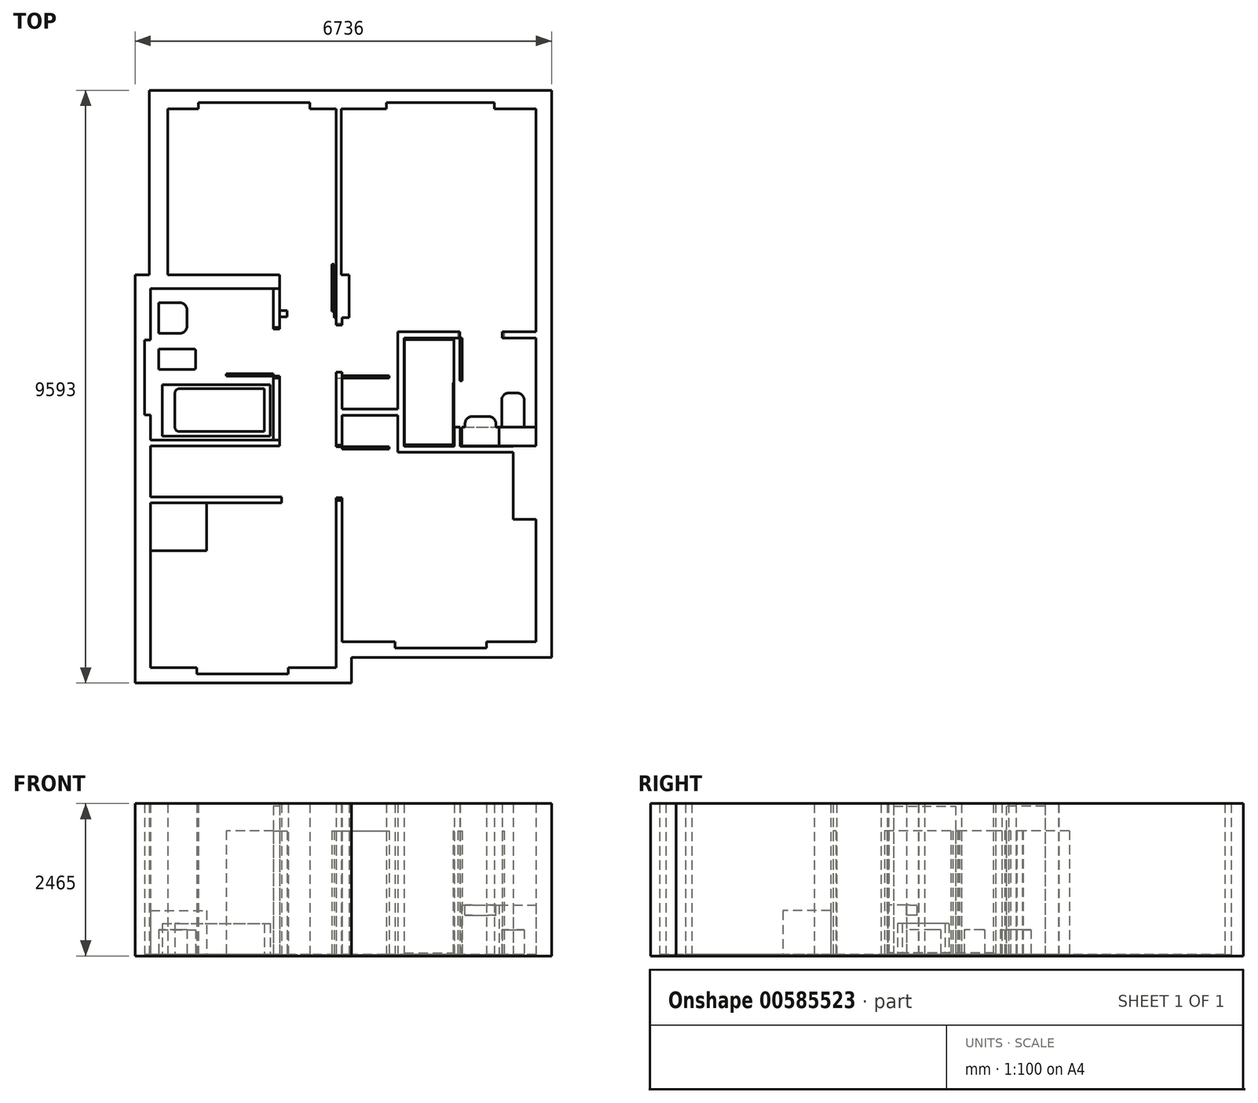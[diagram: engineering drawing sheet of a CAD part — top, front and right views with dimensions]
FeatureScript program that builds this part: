
annotation { "Feature Type Name" : "Feature", "Feature Type Description" : "" }
export const myFeature = defineFeature(function(context is Context, id is Id, definition is map)
    precondition{}
    {
        {
            var Q0;
            Q0=qCreatedBy(makeId("Top.planeOp"),FACE);
            var sketch = newSketch(context, id + "F0", { "sketchPlane" : qUnion([Q0])});
            skLineSegment(sketch, "E0", {"start": v(0, 0) * mm, "end": v(749, 0) * mm});
            skLineSegment(sketch, "E1", {"start": v(749, 0) * mm, "end": v(749, -100) * mm});
            skLineSegment(sketch, "E2", {"start": v(749, -100) * mm, "end": v(2229, -100) * mm});
            skLineSegment(sketch, "E3", {"start": v(2229, -100) * mm, "end": v(2229, 0) * mm});
            skLineSegment(sketch, "E4", {"start": v(2229, 0) * mm, "end": v(3000, 0) * mm});
            skLineSegment(sketch, "E5", {"start": v(3000, 0) * mm, "end": v(3000, 2705) * mm});
            skLineSegment(sketch, "E6", {"start": v(3000, 2705) * mm, "end": v(3100, 2705) * mm});
            skLineSegment(sketch, "E7", {"start": v(3100, 2705) * mm, "end": v(3100, 418) * mm});
            skLineSegment(sketch, "E8", {"start": v(3100, 418) * mm, "end": v(3954, 418) * mm});
            skLineSegment(sketch, "E9", {"start": v(3954, 418) * mm, "end": v(3954, 318) * mm});
            skLineSegment(sketch, "E10", {"start": v(3954, 318) * mm, "end": v(5437, 318) * mm});
            skLineSegment(sketch, "E11", {"start": v(5437, 318) * mm, "end": v(5437, 418) * mm});
            skLineSegment(sketch, "E12", {"start": v(5437, 418) * mm, "end": v(6236, 418) * mm});
            skLineSegment(sketch, "E13", {"start": v(6236, 418) * mm, "end": v(6236, 2400) * mm});
            skLineSegment(sketch, "E14", {"start": v(6236, 2400) * mm, "end": v(5866, 2400) * mm});
            skLineSegment(sketch, "E15", {"start": v(5866, 2400) * mm, "end": v(5866, 3585) * mm});
            skLineSegment(sketch, "E16", {"start": v(5866, 3585) * mm, "end": v(6236, 3585) * mm});
            skLineSegment(sketch, "E17", {"start": v(6236, 3585) * mm, "end": v(6236, 9043) * mm});
            skLineSegment(sketch, "E18", {"start": v(6236, 9043) * mm, "end": v(5559, 9043) * mm});
            skLineSegment(sketch, "E19", {"start": v(5559, 9043) * mm, "end": v(5559, 9143) * mm});
            skLineSegment(sketch, "E20", {"start": v(5559, 9143) * mm, "end": v(3814, 9143) * mm});
            skLineSegment(sketch, "E21", {"start": v(3814, 9143) * mm, "end": v(3814, 9043) * mm});
            skLineSegment(sketch, "E22", {"start": v(3814, 9043) * mm, "end": v(3085, 9043) * mm});
            skLineSegment(sketch, "E23", {"start": v(3085, 9043) * mm, "end": v(3085, 6354) * mm});
            skLineSegment(sketch, "E24", {"start": v(3085, 6354) * mm, "end": v(3210, 6354) * mm});
            skLineSegment(sketch, "E25", {"start": v(3210, 6354) * mm, "end": v(3210, 5663) * mm});
            skLineSegment(sketch, "E26", {"start": v(3210, 5663) * mm, "end": v(3100, 5663) * mm});
            skLineSegment(sketch, "E27", {"start": v(3100, 5663) * mm, "end": v(3100, 3603) * mm});
            skLineSegment(sketch, "E28", {"start": v(3100, 3603) * mm, "end": v(3000, 3603) * mm});
            skLineSegment(sketch, "E29", {"start": v(3000, 3603) * mm, "end": v(3000, 9043) * mm});
            skLineSegment(sketch, "E30", {"start": v(3000, 9043) * mm, "end": v(2575, 9043) * mm});
            skLineSegment(sketch, "E31", {"start": v(2575, 9043) * mm, "end": v(2575, 9143) * mm});
            skLineSegment(sketch, "E32", {"start": v(2575, 9143) * mm, "end": v(775, 9143) * mm});
            skLineSegment(sketch, "E33", {"start": v(775, 9143) * mm, "end": v(775, 9043) * mm});
            skLineSegment(sketch, "E34", {"start": v(775, 9043) * mm, "end": v(280, 9043) * mm});
            skLineSegment(sketch, "E35", {"start": v(280, 9043) * mm, "end": v(280, 6353) * mm});
            skLineSegment(sketch, "E36", {"start": v(280, 6353) * mm, "end": v(2086, 6353) * mm});
            skLineSegment(sketch, "E37", {"start": v(2086, 6353) * mm, "end": v(2086, 6134) * mm});
            skLineSegment(sketch, "E38", {"start": v(2086, 6134) * mm, "end": v(1, 6134) * mm});
            skLineSegment(sketch, "E39", {"start": v(1, 6134) * mm, "end": v(1, 5299) * mm});
            skLineSegment(sketch, "E40", {"start": v(1, 5299) * mm, "end": v(-99, 5299) * mm});
            skLineSegment(sketch, "E41", {"start": v(-99, 5299) * mm, "end": v(-99, 4091) * mm});
            skLineSegment(sketch, "E42", {"start": v(-99, 4091) * mm, "end": v(1, 4091) * mm});
            skLineSegment(sketch, "E43", {"start": v(1, 4091) * mm, "end": v(1, 3685) * mm});
            skLineSegment(sketch, "E44", {"start": v(1, 3685) * mm, "end": v(2086, 3685) * mm});
            skLineSegment(sketch, "E45", {"start": v(2086, 3685) * mm, "end": v(2086, 3585) * mm});
            skLineSegment(sketch, "E46", {"start": v(2086, 3585) * mm, "end": v(0, 3585) * mm});
            skLineSegment(sketch, "E47", {"start": v(0, 3585) * mm, "end": v(0, 2765) * mm});
            skLineSegment(sketch, "E48", {"start": v(0, 2665) * mm, "end": v(6.12, 2665) * mm});
            skLineSegment(sketch, "E49", {"start": v(2119, 2665) * mm, "end": v(2119, 2765) * mm});
            skLineSegment(sketch, "E50", {"start": v(2119, 2765) * mm, "end": v(0, 2765) * mm});
            skLineSegment(sketch, "E51", {"start": v(0, 1892) * mm, "end": v(906, 1892) * mm, "construction": true});
            skLineSegment(sketch, "E52", {"start": v(906, 1892) * mm, "end": v(906, 2665) * mm, "construction": true});
            skLineSegment(sketch, "E53.12", {"start": v(3250, 168) * mm, "end": v(3704, 168) * mm});
            skLineSegment(sketch, "E53.13", {"start": v(3250, -250) * mm, "end": v(3250, 168) * mm});
            skLineSegment(sketch, "E53.14", {"start": v(2479, -250) * mm, "end": v(3250, -250) * mm});
            skLineSegment(sketch, "E53.15", {"start": v(-250, -250) * mm, "end": v(499, -250) * mm});
            skLineSegment(sketch, "E53.19", {"start": v(5687, 168) * mm, "end": v(6486, 168) * mm});
            skLineSegment(sketch, "E53.20", {"start": v(6486, 168) * mm, "end": v(6486, 2650) * mm});
            skLineSegment(sketch, "E53.24", {"start": v(6486, 3335) * mm, "end": v(6486, 9343) * mm});
            skLineSegment(sketch, "E53.28", {"start": v(-250, 6353) * mm, "end": v(-250, -250) * mm});
            skLineSegment(sketch, "E54.0", {"start": v(-20, 9343) * mm, "end": v(-20, 6353) * mm});
            skLineSegment(sketch, "E54.1", {"start": v(775, 9343) * mm, "end": v(-20, 9343) * mm});
            skLineSegment(sketch, "E55", {"start": v(775, 9343) * mm, "end": v(6486, 9343) * mm});
            skLineSegment(sketch, "E56", {"start": v(0, 2765) * mm, "end": v(0, 2765) * mm});
            skLineSegment(sketch, "E57", {"start": v(0, 2665) * mm, "end": v(0, 0) * mm});
            skLineSegment(sketch, "E58", {"start": v(6.12, 2665) * mm, "end": v(2119, 2665) * mm});
            skLineSegment(sketch, "E59", {"start": v(499, -250) * mm, "end": v(2479, -250) * mm});
            skLineSegment(sketch, "E60", {"start": v(3704, 168) * mm, "end": v(5687, 168) * mm});
            skLineSegment(sketch, "E61", {"start": v(6486, 3335) * mm, "end": v(6486, 2650) * mm});
            skLineSegment(sketch, "E62", {"start": v(-250, 6353) * mm, "end": v(-20, 6353) * mm});
            skSolve(sketch);
        }
        {
            var Q0;
            Q0=makeQuery(id+"F0.imprint","IMPRINT",FACE,{"disambiguationData":[TD([[makeQuery(id+"F0.imprint","IMPRINT",EDGE,{"derivedFrom":sQuery(id+"F0.wireOp",EDGE,"E0")}),1.0]])]});
            var sketch = newSketch(context, id + "F1", { "sketchPlane" : qUnion([Q0])});
            skLineSegment(sketch, "E63", {"start": v(3100, 4083) * mm, "end": v(4000, 4083) * mm});
            skLineSegment(sketch, "E64", {"start": v(4000, 4083) * mm, "end": v(4000, 3483) * mm});
            skLineSegment(sketch, "E65", {"start": v(4000, 3483) * mm, "end": v(5866, 3483) * mm});
            skLineSegment(sketch, "E66", {"start": v(4000, 4183) * mm, "end": v(4000, 5433) * mm});
            skLineSegment(sketch, "E67", {"start": v(4000, 5433) * mm, "end": v(6236, 5433) * mm});
            skLineSegment(sketch, "E68", {"start": v(6236, 5333) * mm, "end": v(4100, 5333) * mm});
            skLineSegment(sketch, "E69", {"start": v(4100, 5333) * mm, "end": v(4100, 3583) * mm});
            skLineSegment(sketch, "E70", {"start": v(5866, 3583) * mm, "end": v(5866, 3483) * mm});
            skLineSegment(sketch, "E71", {"start": v(6236, 5333) * mm, "end": v(6236, 5433) * mm});
            skLineSegment(sketch, "E72", {"start": v(3100, 4183) * mm, "end": v(3100, 4083) * mm});
            skLineSegment(sketch, "E73", {"start": v(4100, 3583) * mm, "end": v(4910, 3583) * mm});
            skLineSegment(sketch, "E74.bottom", {"start": v(4105, 5308) * mm, "end": v(4905, 5308) * mm, "construction": true});
            skLineSegment(sketch, "E74.top", {"start": v(4105, 3608) * mm, "end": v(4905, 3608) * mm, "construction": true});
            skLineSegment(sketch, "E74.left", {"start": v(4105, 5308) * mm, "end": v(4105, 3608) * mm, "construction": true});
            skLineSegment(sketch, "E74.right", {"start": v(4905, 5308) * mm, "end": v(4905, 3478) * mm, "construction": true});
            skLineSegment(sketch, "E75", {"start": v(4000, 4183) * mm, "end": v(3100, 4183) * mm});
            skLineSegment(sketch, "E76.bottom", {"start": v(5109.15, 4345.6) * mm, "end": v(5109.15, 5095.6) * mm, "construction": true});
            skLineSegment(sketch, "E76.top", {"start": v(6234.15, 4345.6) * mm, "end": v(6234.15, 5095.6) * mm, "construction": true});
            skLineSegment(sketch, "E76.left", {"start": v(5109.15, 4345.6) * mm, "end": v(6234.15, 4345.6) * mm, "construction": true});
            skLineSegment(sketch, "E76.right", {"start": v(5109.15, 5095.6) * mm, "end": v(6234.15, 5095.6) * mm, "construction": true});
            skLineSegment(sketch, "E77.bottom", {"start": v(5808.64, 3997.9) * mm, "end": v(5808.64, 3497.9) * mm, "construction": true});
            skLineSegment(sketch, "E77.top", {"start": v(5048.64, 3997.9) * mm, "end": v(5048.64, 3497.9) * mm, "construction": true});
            skLineSegment(sketch, "E77.left", {"start": v(5808.64, 3997.9) * mm, "end": v(5048.64, 3997.9) * mm, "construction": true});
            skLineSegment(sketch, "E77.right", {"start": v(5808.64, 3497.9) * mm, "end": v(5048.64, 3497.9) * mm, "construction": true});
            skLineSegment(sketch, "E78", {"start": v(5109.15, 4720.6) * mm, "end": v(6234.15, 4720.6) * mm, "construction": true});
            skLineSegment(sketch, "E79", {"start": v(5428.64, 3997.9) * mm, "end": v(5428.64, 3497.9) * mm, "construction": true});
            skLineSegment(sketch, "E80.bottom", {"start": v(4910, 3890) * mm, "end": v(5010, 3890) * mm});
            skLineSegment(sketch, "E80.left", {"start": v(4910, 3890) * mm, "end": v(4910, 3583) * mm});
            skLineSegment(sketch, "E80.right", {"start": v(5010, 3890) * mm, "end": v(5010, 3583) * mm});
            skLineSegment(sketch, "E81.trimOffspring", {"start": v(5010, 3583) * mm, "end": v(5866, 3583) * mm});
            skSolve(sketch);
        }
        {
            var Q0;
            Q0=qCreatedBy(makeId("Top.planeOp"),FACE);
            var sketch = newSketch(context, id + "F2", { "sketchPlane" : qUnion([Q0])});
            skLineSegment(sketch, "E82.bottom", {"start": v(3000, 5545) * mm, "end": v(3100, 5545) * mm});
            skLineSegment(sketch, "E82.top", {"start": v(3000, 4783) * mm, "end": v(3100, 4783) * mm});
            skLineSegment(sketch, "E82.left", {"start": v(3000, 5545) * mm, "end": v(3000, 4783) * mm});
            skLineSegment(sketch, "E82.right", {"start": v(3100, 5545) * mm, "end": v(3100, 4783) * mm});
            skSolve(sketch);
        }
        {
            var Q0;
            Q0=qCreatedBy(makeId("Top.planeOp"),FACE);
            var sketch = newSketch(context, id + "F3", { "sketchPlane" : qUnion([Q0])});
            skLineSegment(sketch, "E83.bottom", {"start": v(5000, 5433) * mm, "end": v(5690, 5433) * mm});
            skLineSegment(sketch, "E83.top", {"start": v(5000, 5333) * mm, "end": v(5690, 5333) * mm});
            skLineSegment(sketch, "E83.left", {"start": v(5000, 5433) * mm, "end": v(5000, 5333) * mm});
            skLineSegment(sketch, "E83.right", {"start": v(5690, 5433) * mm, "end": v(5690, 5333) * mm});
            skSolve(sketch);
        }
        {
            var Q0;
            Q0=qCreatedBy(makeId("Top.planeOp"),FACE);
            var sketch = newSketch(context, id + "F4", { "sketchPlane" : qUnion([Q0])});
            skLineSegment(sketch, "E84.0", {"start": v(4105, 5308) * mm, "end": v(4905, 5308) * mm});
            skLineSegment(sketch, "E85.0", {"start": v(4105, 5308) * mm, "end": v(4105, 3608) * mm});
            skLineSegment(sketch, "E86.0", {"start": v(4105, 3608) * mm, "end": v(4905, 3608) * mm});
            skLineSegment(sketch, "E87.0", {"start": v(4905, 5308) * mm, "end": v(4905, 3478) * mm});
            skLineSegment(sketch, "E88.bottom", {"start": v(5454.15, 4903.1) * mm, "end": v(5889.15, 4903.1) * mm});
            skLineSegment(sketch, "E88.top", {"start": v(5454.15, 4538.1) * mm, "end": v(5889.15, 4538.1) * mm});
            skLineSegment(sketch, "E88.left", {"start": v(5374.15, 4823.1) * mm, "end": v(5374.15, 4618.1) * mm});
            skLineSegment(sketch, "E88.right", {"start": v(5929.15, 4863.1) * mm, "end": v(5929.15, 4578.1) * mm});
            skLineSegment(sketch, "E89", {"start": v(5374.15, 4720.6) * mm, "end": v(5866, 4720.6) * mm, "construction": true});
            skPoint(sketch, "E90.visualSharp", {"position": v(5374.15, 4903.1) * mm});
            skArc(sketch, "E90.filletArc", {"start": v(5454.15, 4903.1) * mm, "mid": v(5397.58, 4879.66) * mm, "end": v(5374.15, 4823.1) * mm});
            skPoint(sketch, "E91.visualSharp", {"position": v(5374.15, 4538.1) * mm});
            skArc(sketch, "E91.filletArc", {"start": v(5374.15, 4618.1) * mm, "mid": v(5397.58, 4561.53) * mm, "end": v(5454.15, 4538.1) * mm});
            skPoint(sketch, "E92.visualSharp", {"position": v(5866, 4538.1) * mm});
            skArc(sketch, "E92.filletArc", {"start": v(5889.15, 4538.1) * mm, "mid": v(5917.44, 4549.81) * mm, "end": v(5929.15, 4578.1) * mm});
            skPoint(sketch, "E93.visualSharp", {"position": v(5866, 4903.1) * mm});
            skArc(sketch, "E93.filletArc", {"start": v(5929.15, 4863.1) * mm, "mid": v(5917.44, 4891.38) * mm, "end": v(5889.15, 4903.1) * mm});
            skLineSegment(sketch, "E94.bottom", {"start": v(5678.64, 3632.47) * mm, "end": v(5678.64, 3277.47) * mm});
            skLineSegment(sketch, "E94.top", {"start": v(5178.64, 3632.47) * mm, "end": v(5178.64, 3277.47) * mm});
            skLineSegment(sketch, "E94.left", {"start": v(5578.64, 3732.47) * mm, "end": v(5278.64, 3732.47) * mm});
            skLineSegment(sketch, "E94.right", {"start": v(5678.64, 3277.47) * mm, "end": v(5178.64, 3277.47) * mm});
            skLineSegment(sketch, "E95", {"start": v(5428.64, 3732.47) * mm, "end": v(5428.64, 3277.47) * mm, "construction": true});
            skPoint(sketch, "E96.visualSharp", {"position": v(5678.64, 3732.47) * mm});
            skArc(sketch, "E96.filletArc", {"start": v(5678.64, 3632.47) * mm, "mid": v(5649.35, 3703.18) * mm, "end": v(5578.64, 3732.47) * mm});
            skPoint(sketch, "E97.visualSharp", {"position": v(5178.64, 3732.47) * mm});
            skArc(sketch, "E97.filletArc", {"start": v(5278.64, 3732.47) * mm, "mid": v(5207.93, 3703.18) * mm, "end": v(5178.64, 3632.47) * mm});
            skCircle(sketch, "E98", {"center": v(5428.64, 3482.47) * mm, "radius": 38 * mm});
            skCircle(sketch, "E99", {"center": v(5428.64, 2896.26) * mm, "radius": 12.5 * mm});
            skSolve(sketch);
        }
        {
            var Q0;
            Q0=qCreatedBy(makeId("Top.planeOp"),FACE);
            var sketch = newSketch(context, id + "F5", { "sketchPlane" : qUnion([Q0])});
            skLineSegment(sketch, "E100.bottom", {"start": v(2086, 3685) * mm, "end": v(1986, 3685) * mm});
            skLineSegment(sketch, "E100.top", {"start": v(2086, 4685) * mm, "end": v(1986, 4685) * mm});
            skLineSegment(sketch, "E100.left", {"start": v(2086, 3685) * mm, "end": v(2086, 4685) * mm});
            skLineSegment(sketch, "E100.right", {"start": v(1986, 3685) * mm, "end": v(1986, 4685) * mm});
            skLineSegment(sketch, "E101.bottom", {"start": v(1986, 6134) * mm, "end": v(2086, 6134) * mm});
            skLineSegment(sketch, "E101.top", {"start": v(1986, 5507) * mm, "end": v(2086, 5507) * mm});
            skLineSegment(sketch, "E101.left", {"start": v(1986, 6134) * mm, "end": v(1986, 5507) * mm});
            skLineSegment(sketch, "E101.right", {"start": v(2086, 6134) * mm, "end": v(2086, 5507) * mm});
            skSolve(sketch);
        }
        {
            var Q0;
            Q0=makeQuery(id+"F0.imprint","IMPRINT",FACE,{"disambiguationData":[TD([[makeQuery(id+"F0.imprint","IMPRINT",EDGE,{"derivedFrom":sQuery(id+"F0.wireOp",EDGE,"E0")}),-1.0]])]});
            extrude(context, id + "F6", {"entities" : qUnion([Q0]), "depth" : 2440 * mm, "offsetDistance" : 25 * mm});
        }
        {
            var Q0;
            Q0 = qSketchRegion(id + "F1", true);
            var Q1;
            Q1=makeQuery(id+"F0.imprint","IMPRINT",FACE,{"disambiguationData":[TD([[makeQuery(id+"F0.imprint","IMPRINT",EDGE,{"derivedFrom":sQuery(id+"F0.wireOp",EDGE,"E0")}),-1.0]])]});
            var Q2;
            Q2=makeQuery(id+"F0.imprint","IMPRINT",FACE,{"disambiguationData":[TD([[makeQuery(id+"F0.imprint","IMPRINT",EDGE,{"derivedFrom":sQuery(id+"F0.wireOp",EDGE,"E0")}),1.0]])]});
            var Q3;
            Q3=sQuery(id+"F0.wireOp",EDGE,"E53.28");
            var Q4;
            Q4=sQuery(id+"F0.wireOp",EDGE,"E53.15");
            var Q5;
            Q5=sQuery(id+"F0.wireOp",EDGE,"E59");
            var Q6;
            Q6=sQuery(id+"F0.wireOp",EDGE,"E53.14");
            var Q7;
            Q7=sQuery(id+"F0.wireOp",EDGE,"E53.13");
            var Q8;
            Q8=sQuery(id+"F0.wireOp",EDGE,"E53.19");
            var Q9;
            Q9=sQuery(id+"F0.wireOp",EDGE,"E60");
            var Q10;
            Q10=sQuery(id+"F0.wireOp",EDGE,"E53.12");
            var Q11;
            Q11=sQuery(id+"F0.wireOp",EDGE,"E53.20");
            var Q12;
            Q12=sQuery(id+"F0.wireOp",EDGE,"E61");
            var Q13;
            Q13=sQuery(id+"F0.wireOp",EDGE,"E53.24");
            var Q14;
            Q14=sQuery(id+"F0.wireOp",EDGE,"E55");
            var Q15;
            Q15=sQuery(id+"F0.wireOp",EDGE,"E54.1");
            var Q16;
            Q16=sQuery(id+"F0.wireOp",EDGE,"E62");
            var Q17;
            Q17=sQuery(id+"F0.wireOp",EDGE,"E54.0");
            extrude(context, id + "F7", {"entities" : qUnion([Q0, Q1, Q2]), "operationType" : NewBodyOperationType.ADD, "surfaceEntities" : qUnion([Q3, Q4, Q5, Q6, Q7, Q8, Q9, Q10, Q11, Q12, Q13, Q14, Q15, Q16, Q17]), "oppositeDirection" : true, "depth" : 25 * mm, "offsetDistance" : 25 * mm});
        }
        {
            var Q0;
            Q0 = qSketchRegion(id + "F1", true);
            extrude(context, id + "F8", {"entities" : qUnion([Q0]), "operationType" : NewBodyOperationType.ADD, "depth" : 2440 * mm, "offsetDistance" : 25 * mm});
        }
        {
            var Q0;
            Q0 = qSketchRegion(id + "F2", true);
            extrude(context, id + "F9", {"entities" : qUnion([Q0]), "operationType" : NewBodyOperationType.REMOVE, "depth" : 3100 * mm, "offsetDistance" : 25 * mm});
        }
        {
            var Q0;
            Q0 = qSketchRegion(id + "F3", true);
            extrude(context, id + "F10", {"entities" : qUnion([Q0]), "operationType" : NewBodyOperationType.REMOVE, "depth" : 3100 * mm, "offsetDistance" : 25 * mm});
        }
        {
            var Q0;
            Q0 = qSketchRegion(id + "F5", true);
            extrude(context, id + "F11", {"entities" : qUnion([Q0]), "operationType" : NewBodyOperationType.ADD, "depth" : 2400 * mm, "offsetDistance" : 25 * mm});
        }
        {
            var Q0;
            Q0=qCreatedBy(makeId("Top.planeOp"),FACE);
            var sketch = newSketch(context, id + "F12", { "sketchPlane" : qUnion([Q0])});
            skLineSegment(sketch, "E102.bottom", {"start": v(4895, 4608) * mm, "end": v(4905, 4608) * mm});
            skLineSegment(sketch, "E102.top", {"start": v(4895, 3608) * mm, "end": v(4905, 3608) * mm});
            skLineSegment(sketch, "E102.left", {"start": v(4895, 4608) * mm, "end": v(4895, 3608) * mm});
            skLineSegment(sketch, "E102.right", {"start": v(4905, 4608) * mm, "end": v(4905, 3608) * mm});
            skSolve(sketch);
        }
        {
            var Q0;
            Q0 = qSketchRegion(id + "F12", true);
            extrude(context, id + "F13", {"entities" : qUnion([Q0]), "operationType" : NewBodyOperationType.ADD, "depth" : 2000 * mm, "offsetDistance" : 25 * mm});
        }
        {
            var Q0;
            Q0=qCreatedBy(makeId("Top.planeOp"),FACE);
            var sketch = newSketch(context, id + "F14", { "sketchPlane" : qUnion([Q0])});
            skLineSegment(sketch, "E103.bottom", {"start": v(5636, 3890) * mm, "end": v(6236, 3890) * mm});
            skLineSegment(sketch, "E103.top", {"start": v(5636, 3585) * mm, "end": v(6236, 3585) * mm});
            skLineSegment(sketch, "E103.left", {"start": v(5636, 3890) * mm, "end": v(5636, 3585) * mm});
            skLineSegment(sketch, "E103.right", {"start": v(6236, 3890) * mm, "end": v(6236, 3585) * mm});
            skSolve(sketch);
        }
        {
            var Q0;
            Q0 = qSketchRegion(id + "F14", true);
            extrude(context, id + "F15", {"entities" : qUnion([Q0]), "operationType" : NewBodyOperationType.ADD, "depth" : 800 * mm, "offsetDistance" : 25 * mm});
        }
        {
            var Q0;
            Q0=qCreatedBy(makeId("Top.planeOp"),FACE);
            var sketch = newSketch(context, id + "F16", { "sketchPlane" : qUnion([Q0])});
            skLineSegment(sketch, "E104.bottom", {"start": v(5486, 4970) * mm, "end": v(6236, 4970) * mm});
            skLineSegment(sketch, "E104.top", {"start": v(5486, 3890) * mm, "end": v(6236, 3890) * mm});
            skLineSegment(sketch, "E104.left", {"start": v(5486, 4970) * mm, "end": v(5486, 3890) * mm});
            skLineSegment(sketch, "E104.right", {"start": v(6236, 4970) * mm, "end": v(6236, 3890) * mm});
            skLineSegment(sketch, "E105.bottom", {"start": v(5798.5, 4446) * mm, "end": v(5923.5, 4446) * mm});
            skLineSegment(sketch, "E105.top", {"start": v(5678.5, 3891) * mm, "end": v(6043.5, 3891) * mm});
            skLineSegment(sketch, "E105.left", {"start": v(5678.5, 4326) * mm, "end": v(5678.5, 3891) * mm});
            skLineSegment(sketch, "E105.right", {"start": v(6043.5, 4326) * mm, "end": v(6043.5, 3891) * mm});
            skLineSegment(sketch, "E106", {"start": v(5861, 4970) * mm, "end": v(5861, 4446) * mm, "construction": true});
            skPoint(sketch, "E107.visualSharp", {"position": v(5678.5, 4446) * mm});
            skArc(sketch, "E107.filletArc", {"start": v(5798.5, 4446) * mm, "mid": v(5713.65, 4410.85) * mm, "end": v(5678.5, 4326) * mm});
            skPoint(sketch, "E108.visualSharp", {"position": v(6043.5, 4446) * mm});
            skArc(sketch, "E108.filletArc", {"start": v(6043.5, 4326) * mm, "mid": v(6008.35, 4410.85) * mm, "end": v(5923.5, 4446) * mm});
            skSolve(sketch);
        }
        {
            var Q0;
            Q0=qCreatedBy(makeId("Top.planeOp"),FACE);
            var sketch = newSketch(context, id + "F17", { "sketchPlane" : qUnion([Q0])});
            skLineSegment(sketch, "E109.0", {"start": v(5678.5, 4326) * mm, "end": v(5678.5, 3891) * mm});
            skArc(sketch, "E110.0", {"start": v(5798.5, 4446) * mm, "mid": v(5713.65, 4410.85) * mm, "end": v(5678.5, 4326) * mm});
            skLineSegment(sketch, "E111.0", {"start": v(5798.5, 4446) * mm, "end": v(5923.5, 4446) * mm});
            skArc(sketch, "E112.0", {"start": v(6043.5, 4326) * mm, "mid": v(6008.35, 4410.85) * mm, "end": v(5923.5, 4446) * mm});
            skLineSegment(sketch, "E113.0", {"start": v(6043.5, 4326) * mm, "end": v(6043.5, 3891) * mm});
            skLineSegment(sketch, "E114.0", {"start": v(5678.5, 3891) * mm, "end": v(6043.5, 3891) * mm});
            skSolve(sketch);
        }
        {
            var Q0;
            Q0 = qSketchRegion(id + "F17", true);
            extrude(context, id + "F18", {"entities" : qUnion([Q0]), "operationType" : NewBodyOperationType.ADD, "depth" : 400 * mm, "offsetDistance" : 25 * mm});
        }
        {
            var Q0;
            Q0=qCreatedBy(makeId("Top.planeOp"),FACE);
            var sketch = newSketch(context, id + "F19", { "sketchPlane" : qUnion([Q0])});
            skLineSegment(sketch, "E115.bottom", {"start": v(5036, 3890) * mm, "end": v(5636, 3890) * mm});
            skLineSegment(sketch, "E115.top", {"start": v(5036, 3585) * mm, "end": v(5636, 3585) * mm});
            skLineSegment(sketch, "E115.left", {"start": v(5036, 3890) * mm, "end": v(5036, 3585) * mm});
            skLineSegment(sketch, "E115.right", {"start": v(5636, 3890) * mm, "end": v(5636, 3585) * mm});
            skSolve(sketch);
        }
        {
            var Q0;
            Q0=makeQuery(id+"F19.imprint","IMPRINT",FACE,{"disambiguationData":[TD([[makeQuery(id+"F19.imprint","IMPRINT",EDGE,{"derivedFrom":sQuery(id+"F19.wireOp",EDGE,"E115.bottom")}),-1.0]])]});
            extrude(context, id + "F20", {"entities" : qUnion([Q0]), "depth" : 800 * mm, "offsetDistance" : 25 * mm});
        }
        {
            var Q0;
            Q0=makeQuery(id+"F20.opExtrude","CAP_FACE",FACE,{"disambiguationData":[OSD([sQuery(id+"F19.wireOp",EDGE,"E115.bottom"),sQuery(id+"F19.wireOp",EDGE,"E115.top"),sQuery(id+"F19.wireOp",EDGE,"E115.left"),sQuery(id+"F19.wireOp",EDGE,"E115.right")])],"isStart":false});
            var sketch = newSketch(context, id + "F21", { "sketchPlane" : qUnion([Q0])});
            skLineSegment(sketch, "E116.bottom", {"start": v(5206, 4065) * mm, "end": v(5466, 4065) * mm});
            skLineSegment(sketch, "E116.top", {"start": v(5086, 3610) * mm, "end": v(5586, 3610) * mm});
            skLineSegment(sketch, "E116.left", {"start": v(5086, 3945) * mm, "end": v(5086, 3610) * mm});
            skLineSegment(sketch, "E116.right", {"start": v(5586, 3945) * mm, "end": v(5586, 3610) * mm});
            skPoint(sketch, "E117.visualSharp", {"position": v(5086, 4065) * mm});
            skArc(sketch, "E117.filletArc", {"start": v(5206, 4065) * mm, "mid": v(5121.15, 4029.85) * mm, "end": v(5086, 3945) * mm});
            skPoint(sketch, "E118.visualSharp", {"position": v(5586, 4065) * mm});
            skArc(sketch, "E118.filletArc", {"start": v(5586, 3945) * mm, "mid": v(5550.85, 4029.85) * mm, "end": v(5466, 4065) * mm});
            skSolve(sketch);
        }
        {
            var Q0;
            Q0 = qSketchRegion(id + "F21", true);
            extrude(context, id + "F22", {"entities" : qUnion([Q0]), "operationType" : NewBodyOperationType.ADD, "oppositeDirection" : true, "depth" : 170 * mm, "offsetDistance" : 25 * mm});
        }
        {
            var Q0;
            Q0=qCreatedBy(makeId("Top.planeOp"),FACE);
            var sketch = newSketch(context, id + "F23", { "sketchPlane" : qUnion([Q0])});
            skLineSegment(sketch, "E119.bottom", {"start": v(2970, 5763) * mm, "end": v(3000, 5763) * mm});
            skLineSegment(sketch, "E119.top", {"start": v(2970, 5663) * mm, "end": v(3000, 5663) * mm});
            skLineSegment(sketch, "E119.left", {"start": v(2970, 5763) * mm, "end": v(2970, 5663) * mm});
            skLineSegment(sketch, "E119.right", {"start": v(3000, 5763) * mm, "end": v(3000, 5663) * mm});
            skLineSegment(sketch, "E120.bottom", {"start": v(2086, 5775.5) * mm, "end": v(2208, 5775.5) * mm});
            skLineSegment(sketch, "E120.top", {"start": v(2086, 5675.5) * mm, "end": v(2208, 5675.5) * mm});
            skLineSegment(sketch, "E120.left", {"start": v(2086, 5775.5) * mm, "end": v(2086, 5675.5) * mm});
            skLineSegment(sketch, "E120.right", {"start": v(2208, 5775.5) * mm, "end": v(2208, 5675.5) * mm});
            skLineSegment(sketch, "E121.bottom", {"start": v(2932, 6525) * mm, "end": v(2970, 6525) * mm});
            skLineSegment(sketch, "E121.top", {"start": v(2932, 5763) * mm, "end": v(2970, 5763) * mm});
            skLineSegment(sketch, "E121.left", {"start": v(2932, 6525) * mm, "end": v(2932, 5763) * mm});
            skLineSegment(sketch, "E121.right", {"start": v(2970, 6525) * mm, "end": v(2970, 5763) * mm});
            skSolve(sketch);
        }
        {
            var Q0;
            Q0 = qSketchRegion(id + "F23", true);
            extrude(context, id + "F24", {"entities" : qUnion([Q0]), "depth" : 2000 * mm, "offsetDistance" : 25 * mm});
        }
        {
            var Q0;
            Q0=qCreatedBy(makeId("Top.planeOp"),FACE);
            var sketch = newSketch(context, id + "F25", { "sketchPlane" : qUnion([Q0])});
            skLineSegment(sketch, "E122.bottom", {"start": v(1986, 4715) * mm, "end": v(2086, 4715) * mm});
            skLineSegment(sketch, "E122.top", {"start": v(1986, 4685) * mm, "end": v(2086, 4685) * mm});
            skLineSegment(sketch, "E122.left", {"start": v(1986, 4715) * mm, "end": v(1986, 4685) * mm});
            skLineSegment(sketch, "E122.right", {"start": v(2086, 4715) * mm, "end": v(2086, 4685) * mm});
            skLineSegment(sketch, "E123.bottom", {"start": v(1986, 5507) * mm, "end": v(2086, 5507) * mm});
            skLineSegment(sketch, "E123.top", {"start": v(1986, 5477) * mm, "end": v(2086, 5477) * mm});
            skLineSegment(sketch, "E123.left", {"start": v(1986, 5507) * mm, "end": v(1986, 5477) * mm});
            skLineSegment(sketch, "E123.right", {"start": v(2086, 5507) * mm, "end": v(2086, 5477) * mm});
            skLineSegment(sketch, "E124.bottom", {"start": v(1986, 4715) * mm, "end": v(1224, 4715) * mm});
            skLineSegment(sketch, "E124.top", {"start": v(1986, 4753) * mm, "end": v(1224, 4753) * mm});
            skLineSegment(sketch, "E124.left", {"start": v(1986, 4715) * mm, "end": v(1986, 4753) * mm});
            skLineSegment(sketch, "E124.right", {"start": v(1224, 4715) * mm, "end": v(1224, 4753) * mm});
            skSolve(sketch);
        }
        {
            var Q0;
            Q0 = qSketchRegion(id + "F25", true);
            extrude(context, id + "F26", {"entities" : qUnion([Q0]), "depth" : 2000 * mm, "offsetDistance" : 25 * mm});
        }
        {
            var Q0;
            Q0=qCreatedBy(makeId("Top.planeOp"),FACE);
            var sketch = newSketch(context, id + "F27", { "sketchPlane" : qUnion([Q0])});
            skLineSegment(sketch, "E125.bottom", {"start": v(3000, 5575) * mm, "end": v(3100, 5575) * mm});
            skLineSegment(sketch, "E125.top", {"start": v(3000, 5545) * mm, "end": v(3100, 5545) * mm});
            skLineSegment(sketch, "E125.left", {"start": v(3000, 5575) * mm, "end": v(3000, 5545) * mm});
            skLineSegment(sketch, "E125.right", {"start": v(3100, 5575) * mm, "end": v(3100, 5545) * mm});
            skLineSegment(sketch, "E126.bottom", {"start": v(3000, 4783) * mm, "end": v(3100, 4783) * mm});
            skLineSegment(sketch, "E126.top", {"start": v(3000, 4685.04) * mm, "end": v(3100, 4685.04) * mm});
            skLineSegment(sketch, "E126.left", {"start": v(3000, 4783) * mm, "end": v(3000, 4685.04) * mm});
            skLineSegment(sketch, "E126.right", {"start": v(3100, 4783) * mm, "end": v(3100, 4685.04) * mm});
            skLineSegment(sketch, "E127.bottom", {"start": v(3100, 4685.04) * mm, "end": v(3862, 4685.04) * mm});
            skLineSegment(sketch, "E127.top", {"start": v(3100, 4723.04) * mm, "end": v(3862, 4723.04) * mm});
            skLineSegment(sketch, "E127.left", {"start": v(3100, 4685.04) * mm, "end": v(3100, 4723.04) * mm});
            skLineSegment(sketch, "E127.right", {"start": v(3862, 4685.04) * mm, "end": v(3862, 4723.04) * mm});
            skSolve(sketch);
        }
        {
            var Q0;
            Q0 = qSketchRegion(id + "F27", true);
            extrude(context, id + "F28", {"entities" : qUnion([Q0]), "depth" : 2000 * mm, "offsetDistance" : 25 * mm});
        }
        {
            var Q0;
            Q0=qCreatedBy(makeId("Top.planeOp"),FACE);
            var sketch = newSketch(context, id + "F29", { "sketchPlane" : qUnion([Q0])});
            skLineSegment(sketch, "E128.bottom", {"start": v(3000, 3603) * mm, "end": v(3100, 3603) * mm});
            skLineSegment(sketch, "E128.top", {"start": v(3000, 3573) * mm, "end": v(3100, 3573) * mm});
            skLineSegment(sketch, "E128.left", {"start": v(3000, 3603) * mm, "end": v(3000, 3573) * mm});
            skLineSegment(sketch, "E128.right", {"start": v(3100, 3603) * mm, "end": v(3100, 3573) * mm});
            skLineSegment(sketch, "E129.bottom", {"start": v(3000, 2748.96) * mm, "end": v(3100, 2748.96) * mm});
            skLineSegment(sketch, "E129.top", {"start": v(3000, 2705) * mm, "end": v(3100, 2705) * mm});
            skLineSegment(sketch, "E129.left", {"start": v(3000, 2748.96) * mm, "end": v(3000, 2705) * mm});
            skLineSegment(sketch, "E129.right", {"start": v(3100, 2748.96) * mm, "end": v(3100, 2705) * mm});
            skLineSegment(sketch, "E130.bottom", {"start": v(3100, 3573) * mm, "end": v(3860, 3573) * mm});
            skLineSegment(sketch, "E130.top", {"start": v(3100, 3535) * mm, "end": v(3860, 3535) * mm});
            skLineSegment(sketch, "E130.left", {"start": v(3100, 3573) * mm, "end": v(3100, 3535) * mm});
            skLineSegment(sketch, "E130.right", {"start": v(3860, 3573) * mm, "end": v(3860, 3535) * mm});
            skSolve(sketch);
        }
        {
            var Q0;
            Q0 = qSketchRegion(id + "F29", true);
            extrude(context, id + "F30", {"entities" : qUnion([Q0]), "depth" : 2000 * mm, "offsetDistance" : 25 * mm});
        }
        {
            var Q0;
            Q0=makeQuery(id+"F0.imprint","IMPRINT",FACE,{"disambiguationData":[TD([[makeQuery(id+"F0.imprint","IMPRINT",EDGE,{"derivedFrom":sQuery(id+"F0.wireOp",EDGE,"E0")}),1.0]])]});
            var sketch = newSketch(context, id + "F31", { "sketchPlane" : qUnion([Q0])});
            skLineSegment(sketch, "E131.bottom", {"start": v(4970, 5433) * mm, "end": v(5000, 5433) * mm});
            skLineSegment(sketch, "E131.top", {"start": v(4970, 5333) * mm, "end": v(5000, 5333) * mm});
            skLineSegment(sketch, "E131.left", {"start": v(4970, 5433) * mm, "end": v(4970, 5333) * mm});
            skLineSegment(sketch, "E131.right", {"start": v(5000, 5433) * mm, "end": v(5000, 5333) * mm});
            skLineSegment(sketch, "E132.bottom", {"start": v(5690, 5433) * mm, "end": v(5720, 5433) * mm});
            skLineSegment(sketch, "E132.top", {"start": v(5690, 5333) * mm, "end": v(5720, 5333) * mm});
            skLineSegment(sketch, "E132.left", {"start": v(5690, 5433) * mm, "end": v(5690, 5333) * mm});
            skLineSegment(sketch, "E132.right", {"start": v(5720, 5433) * mm, "end": v(5720, 5333) * mm});
            skLineSegment(sketch, "E133.bottom", {"start": v(5000, 5333) * mm, "end": v(5038, 5333) * mm});
            skLineSegment(sketch, "E133.top", {"start": v(5000, 4643) * mm, "end": v(5038, 4643) * mm});
            skLineSegment(sketch, "E133.left", {"start": v(5000, 5333) * mm, "end": v(5000, 4643) * mm});
            skLineSegment(sketch, "E133.right", {"start": v(5038, 5333) * mm, "end": v(5038, 4643) * mm});
            skArc(sketch, "E134", {"start": v(5000, 4643) * mm, "mid": v(5487.9, 4845.1) * mm, "end": v(5690, 5333) * mm, "construction": true});
            skSolve(sketch);
        }
        {
            var Q0;
            Q0 = qSketchRegion(id + "F31", true);
            var Q1;
            Q1 = qConstructionFilter(qBodyType(qCreatedBy(id + "F31" ,EDGE), BodyType.WIRE), ConstructionObject.NO);
            extrude(context, id + "F32", {"entities" : qUnion([Q0]), "surfaceEntities" : qUnion([Q1]), "depth" : 2000 * mm, "offsetDistance" : 25 * mm});
        }
        {
            var Q0;
            Q0=qCreatedBy(makeId("Top.planeOp"),FACE);
            var sketch = newSketch(context, id + "F33", { "sketchPlane" : qUnion([Q0])});
            skLineSegment(sketch, "E135.bottom", {"start": v(189.67, 4577.84) * mm, "end": v(1936.15, 4577.84) * mm});
            skLineSegment(sketch, "E135.top", {"start": v(189.67, 3745.78) * mm, "end": v(1936.15, 3745.78) * mm});
            skLineSegment(sketch, "E135.left", {"start": v(189.67, 4577.84) * mm, "end": v(189.67, 3745.78) * mm});
            skLineSegment(sketch, "E135.right", {"start": v(1936.15, 4577.84) * mm, "end": v(1936.15, 3745.78) * mm});
            skLineSegment(sketch, "E136.bottom", {"start": v(467.05, 4512.91) * mm, "end": v(1838.74, 4512.91) * mm});
            skLineSegment(sketch, "E136.top", {"start": v(467.05, 3820.72) * mm, "end": v(1838.74, 3820.72) * mm});
            skLineSegment(sketch, "E136.left", {"start": v(392.05, 4437.91) * mm, "end": v(392.05, 3895.72) * mm});
            skLineSegment(sketch, "E136.right", {"start": v(1838.74, 4512.91) * mm, "end": v(1838.74, 3820.72) * mm});
            skPoint(sketch, "E137.visualSharp", {"position": v(392.05, 4512.91) * mm});
            skArc(sketch, "E137.filletArc", {"start": v(467.05, 4512.91) * mm, "mid": v(414.02, 4490.95) * mm, "end": v(392.05, 4437.91) * mm});
            skPoint(sketch, "E138.visualSharp", {"position": v(392.05, 3820.72) * mm});
            skArc(sketch, "E138.filletArc", {"start": v(392.05, 3895.72) * mm, "mid": v(414.02, 3842.68) * mm, "end": v(467.05, 3820.72) * mm});
            skSolve(sketch);
        }
        {
            var Q0;
            Q0 = qSketchRegion(id + "F33", true);
            extrude(context, id + "F34", {"entities" : qUnion([Q0]), "depth" : 500 * mm, "offsetDistance" : 25 * mm});
        }
        {
            var Q0;
            Q0=qCreatedBy(makeId("Top.planeOp"),FACE);
            var sketch = newSketch(context, id + "F35", { "sketchPlane" : qUnion([Q0])});
            skLineSegment(sketch, "E139.bottom", {"start": v(0, 2666.53) * mm, "end": v(906, 2666.53) * mm});
            skLineSegment(sketch, "E139.top", {"start": v(0, 1892) * mm, "end": v(906, 1892) * mm});
            skLineSegment(sketch, "E139.left", {"start": v(0, 2666.53) * mm, "end": v(0, 1892) * mm});
            skLineSegment(sketch, "E139.right", {"start": v(906, 2666.53) * mm, "end": v(906, 1892) * mm});
            skSolve(sketch);
        }
        {
            var Q0;
            Q0 = qSketchRegion(id + "F35", true);
            extrude(context, id + "F36", {"entities" : qUnion([Q0]), "operationType" : NewBodyOperationType.ADD, "depth" : 706 * mm, "offsetDistance" : 25 * mm});
        }
        {
            var Q0;
            Q0=qCreatedBy(makeId("Top.planeOp"),FACE);
            var sketch = newSketch(context, id + "F37", { "sketchPlane" : qUnion([Q0])});
            skLineSegment(sketch, "E140.bottom", {"start": v(4105, 5308) * mm, "end": v(4905, 5308) * mm});
            skLineSegment(sketch, "E140.top", {"start": v(4105, 3608) * mm, "end": v(4905, 3608) * mm});
            skLineSegment(sketch, "E140.left", {"start": v(4105, 5308) * mm, "end": v(4105, 3608) * mm});
            skLineSegment(sketch, "E140.right", {"start": v(4905, 5308) * mm, "end": v(4905, 3608) * mm});
            skSolve(sketch);
        }
        {
            var Q0;
            Q0 = qSketchRegion(id + "F37", true);
            extrude(context, id + "F38", {"entities" : qUnion([Q0]), "operationType" : NewBodyOperationType.ADD, "depth" : 25 * mm, "offsetDistance" : 25 * mm});
        }
        {
            var Q0;
            Q0=qCreatedBy(makeId("Top.planeOp"),FACE);
            var sketch = newSketch(context, id + "F39", { "sketchPlane" : qUnion([Q0])});
            skLineSegment(sketch, "E141.bottom", {"start": v(588.25, 5787.71) * mm, "end": v(588.25, 5527.71) * mm});
            skLineSegment(sketch, "E141.top", {"start": v(133.25, 5907.71) * mm, "end": v(133.25, 5407.71) * mm});
            skLineSegment(sketch, "E141.left", {"start": v(468.25, 5907.71) * mm, "end": v(133.25, 5907.71) * mm});
            skLineSegment(sketch, "E141.right", {"start": v(468.25, 5407.71) * mm, "end": v(133.25, 5407.71) * mm});
            skPoint(sketch, "E142.visualSharp", {"position": v(588.25, 5907.71) * mm});
            skArc(sketch, "E142.filletArc", {"start": v(588.25, 5787.71) * mm, "mid": v(553.1, 5872.57) * mm, "end": v(468.25, 5907.71) * mm});
            skPoint(sketch, "E143.visualSharp", {"position": v(588.25, 5407.71) * mm});
            skArc(sketch, "E143.filletArc", {"start": v(468.25, 5407.71) * mm, "mid": v(553.1, 5442.86) * mm, "end": v(588.25, 5527.71) * mm});
            skLineSegment(sketch, "E144.bottom", {"start": v(133.25, 5154.2) * mm, "end": v(708.52, 5154.2) * mm});
            skLineSegment(sketch, "E144.top", {"start": v(133.25, 4828.37) * mm, "end": v(708.52, 4828.37) * mm});
            skLineSegment(sketch, "E144.left", {"start": v(133.25, 5154.2) * mm, "end": v(133.25, 4828.37) * mm});
            skLineSegment(sketch, "E144.right", {"start": v(728.52, 5134.2) * mm, "end": v(728.52, 4848.37) * mm});
            skPoint(sketch, "E145.visualSharp", {"position": v(728.52, 5154.2) * mm});
            skArc(sketch, "E145.filletArc", {"start": v(728.52, 5134.2) * mm, "mid": v(722.66, 5148.34) * mm, "end": v(708.52, 5154.2) * mm});
            skPoint(sketch, "E146.visualSharp", {"position": v(728.52, 4828.37) * mm});
            skArc(sketch, "E146.filletArc", {"start": v(708.52, 4828.37) * mm, "mid": v(722.66, 4834.23) * mm, "end": v(728.52, 4848.37) * mm});
            skSolve(sketch);
        }
        {
            var Q0;
            Q0 = qSketchRegion(id + "F39", true);
            extrude(context, id + "F40", {"entities" : qUnion([Q0]), "operationType" : NewBodyOperationType.ADD, "depth" : 400 * mm, "offsetDistance" : 25 * mm});
        }
    });
